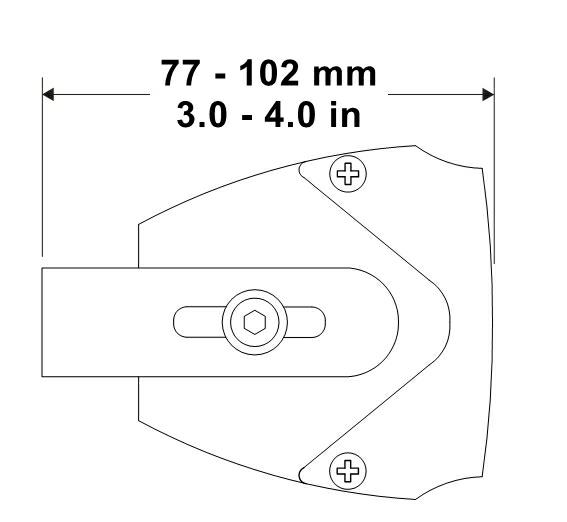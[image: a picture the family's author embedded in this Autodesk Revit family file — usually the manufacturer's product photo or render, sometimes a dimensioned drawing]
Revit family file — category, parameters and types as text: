
# Revit family: Electronics_Desono_Biamp_Two-Way-Column-Loudspeaker_COLS41
name_source: partatom
category: Communication Devices
units: mm (PartAtom-declared; Revit-internal decimal feet)

## family parameters
Cut with Voids When Loaded = No
Host = Face
Maintain Annotation Orientation = No
OmniClass Number = 23.85.10.11.14.14.14
OmniClass Title = Loudspeakers
Part Type = Normal
Room Calculation Point = No
Round Connector Dimension = Use Diameter
Shared = No

## types (1)
- COLS41
    Bracket Material = Biamp - Metal - White
    Connector Description = Terminal block; Low impedance 8 ohms; 70V/100V operation
    Continuous Power Handling Nominal Impedance = 13V; 20W @ 8Ω (80W peak)
    Controls = None; select transformer tap or low impedance input via terminal block wiring
    Default Elevation = 4' - 0"
    Depth = 0' - 2 1/2"
    Description = Desono™ COLS41 Two-Way 4 x 2 Column Loudspeaker
    Environmental = IP66 per IEC 60529
    Grill Material = Biamp - Plastic - White(Grid)
    Height = 1' - 3 1/2"
    Housing Material = Biamp - Plastic - White
    Input Connection = Multi-position pass-through, screw-down terminal block
    Manufacturer = Biamp
    Model = COLS41
    Mounting Provisions = Adjustable tilt L-bracket
    Nominal Beamwidth (H x V) = 150° x 20°
    Nominal Maximum SPL @ 1m = Peak - 106dB; Continuous - 100dB
    Nominal Sensitivity @ 1m = 1W - 87dB; 2.83V - 87dB
    Operating Environment = Indoor/Outdoor
    Operating Mode = Passive
    Operating Range 2 (-10dB) = 175 Hz to 22 kHz
    Product Documentation Link = https://downloads.biamp.com
    Product Page URL = https://www.biamp.com
    Product data url = https://www.bimobject.com
    Recommended Amplifers = 20W - 40W @ 8Ω (13V - 18V)
    Shipping Weight = 4.85 lb
    Transducers = LF 4 x 2 (51 mm) coated paper cone HF 1 x 1 (25 mm) soft dome
    Transformer = 70V: 20W, 10W, 5W, 2.5W; 100V: 20W, 10W, 5W
    URL = https://www.biamp.com
    Weight = 4.41 lb
    Width = 0' - 2 1/2"

## geometry (parser evidence)
native form markers: Sweep x5
no freeform markers — native parametric forms only
